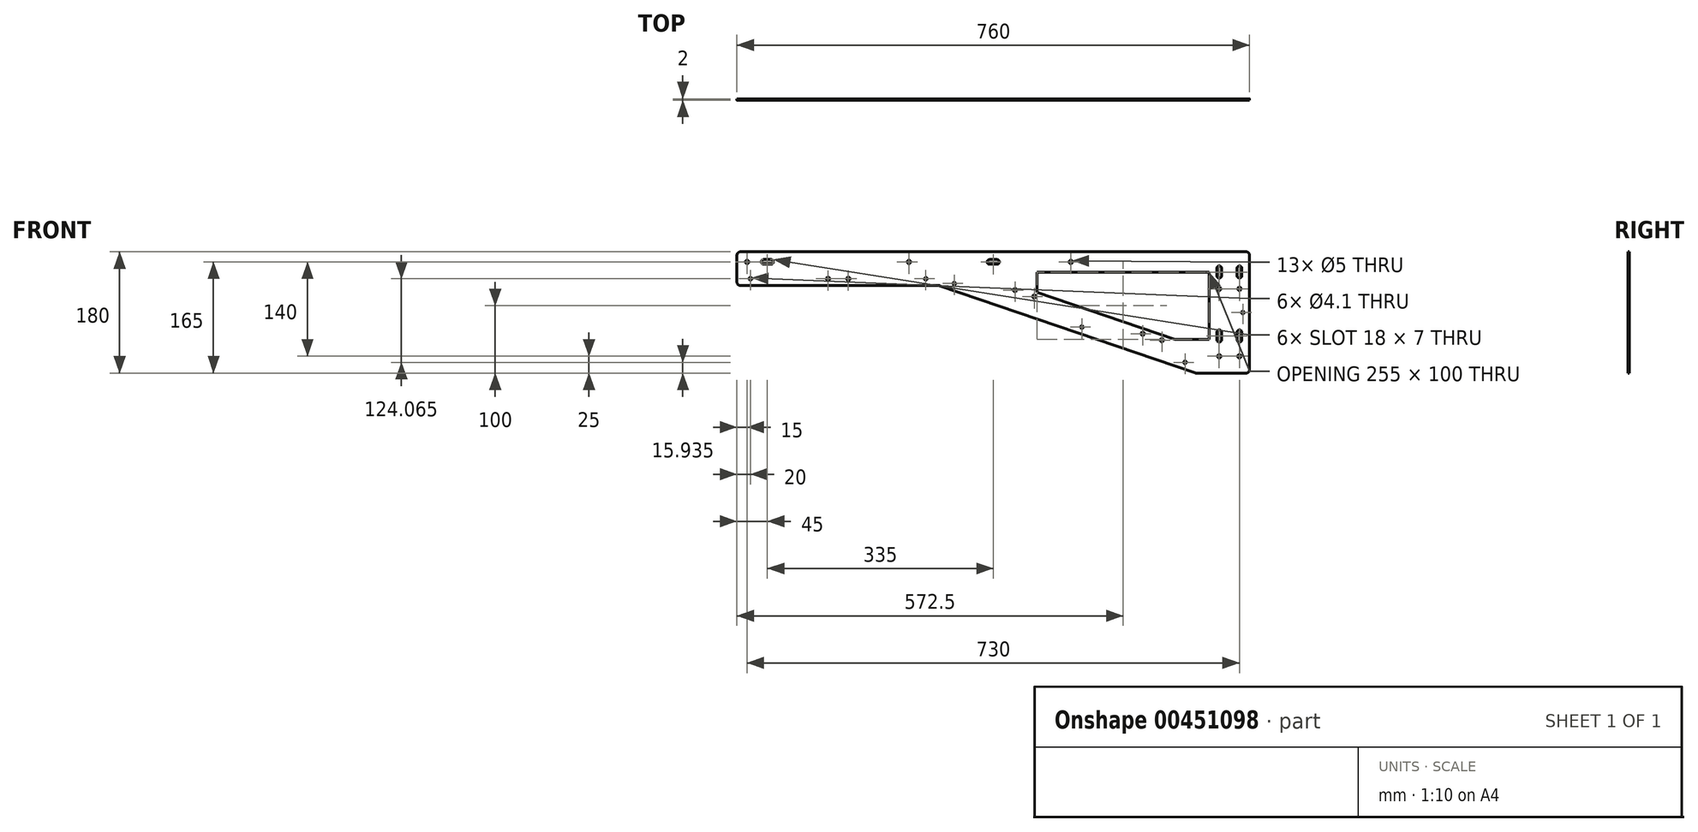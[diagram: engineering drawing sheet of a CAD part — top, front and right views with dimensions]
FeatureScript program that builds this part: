
annotation { "Feature Type Name" : "Feature", "Feature Type Description" : "" }
export const myFeature = defineFeature(function(context is Context, id is Id, definition is map)
    precondition{}
    {
        {
            var Q0;
            Q0=qCreatedBy(makeId("Front.planeOp"),FACE);
            var sketch = newSketch(context, id + "F0", { "sketchPlane" : qUnion([Q0])});
            skLineSegment(sketch, "E0", {"start": v(-760, 180) * mm, "end": v(-760, 130) * mm});
            skLineSegment(sketch, "E1", {"start": v(-760, 130) * mm, "end": v(-460, 130) * mm});
            skLineSegment(sketch, "E2", {"start": v(-460, 130) * mm, "end": v(-80, 0) * mm});
            skLineSegment(sketch, "E3", {"start": v(-80, 0) * mm, "end": v(0, 0) * mm});
            skLineSegment(sketch, "E4", {"start": v(0, 0) * mm, "end": v(0, 180) * mm});
            skLineSegment(sketch, "E5", {"start": v(0, 180) * mm, "end": v(-760, 180) * mm});
            skSolve(sketch);
        }
        {
            var Q0;
            Q0 = qSketchRegion(id + "F0", true);
            extrude(context, id + "F1", {"entities" : qUnion([Q0]), "depth" : 2 * mm, "offsetDistance" : 25 * mm});
        }
        {
            var Q0;
            Q0=makeQuery(id+"F1.opExtrude","CAP_FACE",FACE,{"disambiguationData":[OSD([sQuery(id+"F0.wireOp",EDGE,"E0"),sQuery(id+"F0.wireOp",EDGE,"E1"),sQuery(id+"F0.wireOp",EDGE,"E2"),sQuery(id+"F0.wireOp",EDGE,"E3"),sQuery(id+"F0.wireOp",EDGE,"E4"),sQuery(id+"F0.wireOp",EDGE,"E5")])],"isStart":false});
            var sketch = newSketch(context, id + "F2", { "sketchPlane" : qUnion([Q0])});
            skCircle(sketch, "E6", {"center": v(-15, 25) * mm, "radius": 2.5 * mm});
            skCircle(sketch, "E7", {"center": v(-45, 25) * mm, "radius": 2.5 * mm});
            skCircle(sketch, "E8", {"center": v(-15, 165) * mm, "radius": 2.5 * mm, "construction": true});
            skCircle(sketch, "E9", {"center": v(-45, 165) * mm, "radius": 2.5 * mm, "construction": true});
            skCircle(sketch, "E10", {"center": v(-265, 165) * mm, "radius": 2.5 * mm});
            skCircle(sketch, "E11", {"center": v(-505, 165) * mm, "radius": 2.5 * mm});
            skCircle(sketch, "E12", {"center": v(-745, 165) * mm, "radius": 2.5 * mm});
            skCircle(sketch, "E13", {"center": v(-347.62, 123.26) * mm, "radius": 2.5 * mm});
            skCircle(sketch, "E14", {"center": v(-319.23, 113.55) * mm, "radius": 2.5 * mm});
            skCircle(sketch, "E15", {"center": v(-158.38, 58.52) * mm, "radius": 2.5 * mm});
            skCircle(sketch, "E16", {"center": v(-130, 48.81) * mm, "radius": 2.5 * mm});
            skLineSegment(sketch, "E17", {"start": v(-369.53, 130.76) * mm, "end": v(-99.6, 38.41) * mm, "construction": true});
            skCircle(sketch, "E18", {"center": v(-625, 140) * mm, "radius": 2.5 * mm});
            skCircle(sketch, "E19", {"center": v(-595, 140) * mm, "radius": 2.5 * mm});
            skCircle(sketch, "E20", {"center": v(-15, 125) * mm, "radius": 2.5 * mm});
            skCircle(sketch, "E21", {"center": v(-45, 125) * mm, "radius": 2.5 * mm});
            skCircle(sketch, "E22", {"center": v(-740, 140) * mm, "radius": 2.05 * mm});
            skCircle(sketch, "E23", {"center": v(-480, 140) * mm, "radius": 2.05 * mm});
            skCircle(sketch, "E24", {"center": v(-437.84, 132.99) * mm, "radius": 2.05 * mm});
            skLineSegment(sketch, "E25", {"start": v(-448.75, 126.15) * mm, "end": v(-460, 130) * mm, "construction": true});
            skLineSegment(sketch, "E26", {"start": v(-460, 130) * mm, "end": v(-456, 141.68) * mm, "construction": true});
            skCircle(sketch, "E27", {"center": v(-248.6, 68.25) * mm, "radius": 2.05 * mm});
            skCircle(sketch, "E28", {"center": v(-95.69, 15.94) * mm, "radius": 2.05 * mm});
            skLineSegment(sketch, "E29", {"start": v(-84.94, 1.7) * mm, "end": v(-80, 0) * mm, "construction": true});
            skLineSegment(sketch, "E30", {"start": v(-80, 0) * mm, "end": v(-74.23, 16.87) * mm, "construction": true});
            skCircle(sketch, "E31", {"center": v(-10, 90) * mm, "radius": 2.05 * mm});
            skLineSegment(sketch, "E32.bottom", {"start": v(-709.5, 161.5) * mm, "end": v(-720.5, 161.5) * mm});
            skLineSegment(sketch, "E32.top", {"start": v(-709.5, 168.5) * mm, "end": v(-720.5, 168.5) * mm});
            skLineSegment(sketch, "E32.left", {"start": v(-709.5, 161.5) * mm, "end": v(-709.5, 168.5) * mm, "construction": true});
            skLineSegment(sketch, "E32.right", {"start": v(-720.5, 161.5) * mm, "end": v(-720.5, 168.5) * mm, "construction": true});
            skPoint(sketch, "E32.middle", {"position": v(-715, 165) * mm});
            skArc(sketch, "E33", {"start": v(-720.5, 168.5) * mm, "mid": v(-724, 165) * mm, "end": v(-720.5, 161.5) * mm});
            skArc(sketch, "E34", {"start": v(-709.5, 161.5) * mm, "mid": v(-706, 165) * mm, "end": v(-709.5, 168.5) * mm});
            skLineSegment(sketch, "E35.bottom", {"start": v(-41.5, 155.5) * mm, "end": v(-41.5, 144.5) * mm});
            skLineSegment(sketch, "E35.top", {"start": v(-48.5, 155.5) * mm, "end": v(-48.5, 144.5) * mm});
            skLineSegment(sketch, "E35.left", {"start": v(-41.5, 155.5) * mm, "end": v(-48.5, 155.5) * mm, "construction": true});
            skLineSegment(sketch, "E35.right", {"start": v(-41.5, 144.5) * mm, "end": v(-48.5, 144.5) * mm, "construction": true});
            skPoint(sketch, "E35.middle", {"position": v(-45, 150) * mm});
            skArc(sketch, "E36", {"start": v(-48.5, 144.5) * mm, "mid": v(-45, 141) * mm, "end": v(-41.5, 144.5) * mm});
            skArc(sketch, "E37", {"start": v(-41.5, 155.5) * mm, "mid": v(-45, 159) * mm, "end": v(-48.5, 155.5) * mm});
            skLineSegment(sketch, "E38.bottom", {"start": v(-374.5, 161.5) * mm, "end": v(-385.5, 161.5) * mm});
            skLineSegment(sketch, "E38.top", {"start": v(-374.5, 168.5) * mm, "end": v(-385.5, 168.5) * mm});
            skLineSegment(sketch, "E38.left", {"start": v(-374.5, 161.5) * mm, "end": v(-374.5, 168.5) * mm, "construction": true});
            skLineSegment(sketch, "E38.right", {"start": v(-385.5, 161.5) * mm, "end": v(-385.5, 168.5) * mm, "construction": true});
            skPoint(sketch, "E38.middle", {"position": v(-380, 165) * mm});
            skArc(sketch, "E39", {"start": v(-385.5, 168.5) * mm, "mid": v(-389, 165) * mm, "end": v(-385.5, 161.5) * mm});
            skArc(sketch, "E40", {"start": v(-374.5, 161.5) * mm, "mid": v(-371, 165) * mm, "end": v(-374.5, 168.5) * mm});
            skLineSegment(sketch, "E41.bottom", {"start": v(-11.5, 155.5) * mm, "end": v(-11.5, 144.5) * mm});
            skLineSegment(sketch, "E41.top", {"start": v(-18.5, 155.5) * mm, "end": v(-18.5, 144.5) * mm});
            skLineSegment(sketch, "E41.left", {"start": v(-11.5, 155.5) * mm, "end": v(-18.5, 155.5) * mm, "construction": true});
            skLineSegment(sketch, "E41.right", {"start": v(-11.5, 144.5) * mm, "end": v(-18.5, 144.5) * mm, "construction": true});
            skPoint(sketch, "E41.middle", {"position": v(-15, 150) * mm});
            skArc(sketch, "E42", {"start": v(-18.5, 144.5) * mm, "mid": v(-15, 141) * mm, "end": v(-11.5, 144.5) * mm});
            skArc(sketch, "E43", {"start": v(-11.5, 155.5) * mm, "mid": v(-15, 159) * mm, "end": v(-18.5, 155.5) * mm});
            skLineSegment(sketch, "E44.bottom", {"start": v(-41.5, 60.5) * mm, "end": v(-41.5, 49.5) * mm});
            skLineSegment(sketch, "E44.top", {"start": v(-48.5, 60.5) * mm, "end": v(-48.5, 49.5) * mm});
            skLineSegment(sketch, "E44.left", {"start": v(-41.5, 60.5) * mm, "end": v(-48.5, 60.5) * mm, "construction": true});
            skLineSegment(sketch, "E44.right", {"start": v(-41.5, 49.5) * mm, "end": v(-48.5, 49.5) * mm, "construction": true});
            skPoint(sketch, "E44.middle", {"position": v(-45, 55) * mm});
            skArc(sketch, "E45", {"start": v(-48.5, 49.5) * mm, "mid": v(-45, 46) * mm, "end": v(-41.5, 49.5) * mm});
            skArc(sketch, "E46", {"start": v(-41.5, 60.5) * mm, "mid": v(-45, 64) * mm, "end": v(-48.5, 60.5) * mm});
            skLineSegment(sketch, "E47.bottom", {"start": v(-11.5, 60.5) * mm, "end": v(-11.5, 49.5) * mm});
            skLineSegment(sketch, "E47.top", {"start": v(-18.5, 60.5) * mm, "end": v(-18.5, 49.5) * mm});
            skLineSegment(sketch, "E47.left", {"start": v(-11.5, 60.5) * mm, "end": v(-18.5, 60.5) * mm, "construction": true});
            skLineSegment(sketch, "E47.right", {"start": v(-11.5, 49.5) * mm, "end": v(-18.5, 49.5) * mm, "construction": true});
            skPoint(sketch, "E47.middle", {"position": v(-15, 55) * mm});
            skArc(sketch, "E48", {"start": v(-18.5, 49.5) * mm, "mid": v(-15, 46) * mm, "end": v(-11.5, 49.5) * mm});
            skArc(sketch, "E49", {"start": v(-11.5, 60.5) * mm, "mid": v(-15, 64) * mm, "end": v(-18.5, 60.5) * mm});
            skSolve(sketch);
        }
        {
            var Q0;
            Q0 = qSketchRegion(id + "F2", true);
            extrude(context, id + "F3", {"entities" : qUnion([Q0]), "operationType" : NewBodyOperationType.REMOVE, "oppositeDirection" : true, "depth" : 25 * mm, "offsetDistance" : 25 * mm});
        }
        {
            var Q0;
            Q0=makeQuery(id+"F1.opExtrude","SWEPT_EDGE",EDGE,{"disambiguationData":[OSD([sQuery(id+"F0.wireOp",EDGE,"E0"),sQuery(id+"F0.wireOp",EDGE,"E5")])]});
            var Q1;
            Q1=makeQuery(id+"F1.opExtrude","SWEPT_EDGE",EDGE,{"disambiguationData":[OSD([sQuery(id+"F0.wireOp",EDGE,"E0"),sQuery(id+"F0.wireOp",EDGE,"E1")])]});
            var Q2;
            Q2=makeQuery(id+"F1.opExtrude","SWEPT_EDGE",EDGE,{"disambiguationData":[OSD([sQuery(id+"F0.wireOp",EDGE,"E1"),sQuery(id+"F0.wireOp",EDGE,"E2")])]});
            var Q3;
            Q3=makeQuery(id+"F1.opExtrude","SWEPT_EDGE",EDGE,{"disambiguationData":[OSD([sQuery(id+"F0.wireOp",EDGE,"E2"),sQuery(id+"F0.wireOp",EDGE,"E3")])]});
            var Q4;
            Q4=makeQuery(id+"F1.opExtrude","SWEPT_EDGE",EDGE,{"disambiguationData":[OSD([sQuery(id+"F0.wireOp",EDGE,"E3"),sQuery(id+"F0.wireOp",EDGE,"E4")])]});
            var Q5;
            Q5=makeQuery(id+"F1.opExtrude","SWEPT_EDGE",EDGE,{"disambiguationData":[OSD([sQuery(id+"F0.wireOp",EDGE,"E4"),sQuery(id+"F0.wireOp",EDGE,"E5")])]});
            fillet(context, id + "F4", {"entities" : qUnion([Q0, Q1, Q2, Q3, Q4, Q5]), "radius" : 5 * mm, "tangentPropagation" : true, "allowEdgeOverflow" : false});
        }
        {
            var Q0;
            Q0=makeQuery(id+"F1.opExtrude","CAP_FACE",FACE,{"disambiguationData":[OSD([sQuery(id+"F0.wireOp",EDGE,"E0"),sQuery(id+"F0.wireOp",EDGE,"E1"),sQuery(id+"F0.wireOp",EDGE,"E2"),sQuery(id+"F0.wireOp",EDGE,"E3"),sQuery(id+"F0.wireOp",EDGE,"E4"),sQuery(id+"F0.wireOp",EDGE,"E5")])],"isStart":false});
            var sketch = newSketch(context, id + "F5", { "sketchPlane" : qUnion([Q0])});
            skLineSegment(sketch, "E50", {"start": v(-315, 150) * mm, "end": v(-60, 150) * mm});
            skLineSegment(sketch, "E51", {"start": v(-60, 150) * mm, "end": v(-60, 50) * mm});
            skLineSegment(sketch, "E52", {"start": v(-60, 50) * mm, "end": v(-110.38, 50) * mm});
            skLineSegment(sketch, "E53", {"start": v(-110.38, 50) * mm, "end": v(-315, 120) * mm});
            skLineSegment(sketch, "E54", {"start": v(-315, 120) * mm, "end": v(-315, 150) * mm});
            skSolve(sketch);
        }
        {
            var Q0;
            Q0 = qSketchRegion(id + "F5", true);
            extrude(context, id + "F6", {"entities" : qUnion([Q0]), "operationType" : NewBodyOperationType.REMOVE, "oppositeDirection" : true, "depth" : 25 * mm, "offsetDistance" : 25 * mm});
        }
    });
